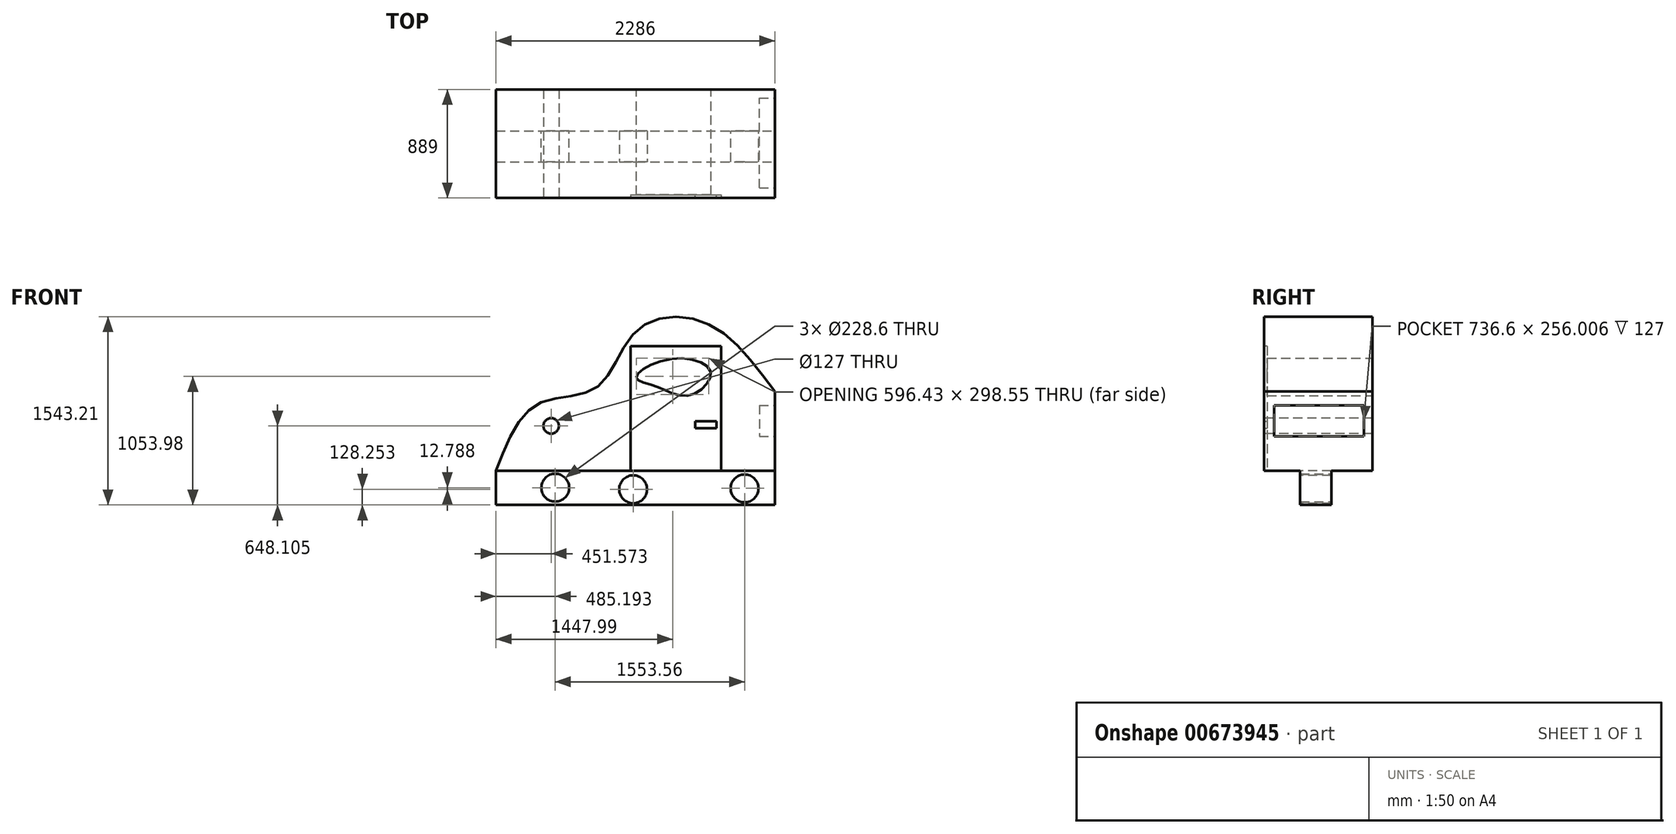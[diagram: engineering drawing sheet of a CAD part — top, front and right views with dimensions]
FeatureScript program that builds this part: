
annotation { "Feature Type Name" : "Feature", "Feature Type Description" : "" }
export const myFeature = defineFeature(function(context is Context, id is Id, definition is map)
    precondition{}
    {
        {
            var Q0;
            Q0=qCreatedBy(makeId("Top.planeOp"),FACE);
            var sketch = newSketch(context, id + "F0", { "sketchPlane" : qUnion([Q0])});
            skLineSegment(sketch, "E0.bottom", {"start": v(-627.65, 592.56) * mm, "end": v(1658.35, 592.56) * mm});
            skLineSegment(sketch, "E0.top", {"start": v(-627.65, -296.44) * mm, "end": v(1658.35, -296.44) * mm});
            skLineSegment(sketch, "E0.left", {"start": v(-627.65, 592.56) * mm, "end": v(-627.65, -296.44) * mm});
            skLineSegment(sketch, "E0.right", {"start": v(1658.35, 592.56) * mm, "end": v(1658.35, -296.44) * mm});
            skSolve(sketch);
        }
        {
            var Q0;
            Q0=makeQuery(id+"F0.imprint","IMPRINT",FACE,{"disambiguationData":[TD([[makeQuery(id+"F0.imprint","IMPRINT",EDGE,{"derivedFrom":sQuery(id+"F0.wireOp",EDGE,"E0.bottom")}),-1.0]])]});
            extrude(context, id + "F1", {"entities" : qUnion([Q0]), "depth" : 1778 * mm, "offsetDistance" : 25.4 * mm});
        }
        {
            var Q0;
            Q0=makeQuery(id+"F1.opExtrude","SWEPT_FACE",FACE,{"disambiguationData":[OSD([sQuery(id+"F0.wireOp",EDGE,"E0.top")])]});
            var sketch = newSketch(context, id + "F2", { "sketchPlane" : qUnion([Q0])});
            skFitSpline(sketch, "E1", {"points": [v(-627.65, 0) * mm, v(-288.97, 545.87) * mm, v(200.39, 685.84) * mm, v(521.68, 1145.9) * mm, v(1081.4, 1218.44) * mm, v(1658.35, 650.05) * mm], "startDerivative": vector(1263.53, 3349.31) * mm, "endDerivative": vector(2269, -3098.13) * mm});
            skSolve(sketch);
        }
        {
            var Q0;
            Q0=makeQuery(id+"F2.imprint","IMPRINT",FACE,{"disambiguationData":[TD([[makeQuery(id+"F2.imprint","IMPRINT",EDGE,{"derivedFrom":sQuery(id+"F2.wireOp",EDGE,"4d44a828-738e-46ed-b581-61caa8d3ac53")}),1.0]])]});
            var Q1;
            {var subQ0=sQuery(id+"F2.wireOp",EDGE,"E1");Q1=makeQuery(id+"F2.imprint","IMPRINT",FACE,{"disambiguationData":[TD([[makeQuery(id+"F2.imprint","IMPRINT",EDGE,{"derivedFrom":subQ0}),1.0]])]});}
            extrude(context, id + "F3", {"entities" : qUnion([Q0, Q1]), "operationType" : NewBodyOperationType.REMOVE, "oppositeDirection" : true, "depth" : 889 * mm, "offsetDistance" : 25.4 * mm});
        }
        {
            var Q0;
            Q0=makeQuery(id+"F1.opExtrude","SWEPT_FACE",FACE,{"disambiguationData":[OSD([sQuery(id+"F0.wireOp",EDGE,"E0.top")])]});
            var sketch = newSketch(context, id + "F4", { "sketchPlane" : qUnion([Q0])});
            skFitSpline(sketch, "E2", {"points": [v(522.12, 767.1) * mm, v(816.35, 920.03) * mm, v(1133.81, 805.82) * mm, v(963.47, 621.93) * mm, v(678.91, 693.55) * mm, v(522.12, 767.1) * mm]});
            skSolve(sketch);
        }
        {
            var Q0;
            Q0=makeQuery(id+"F4.imprint","IMPRINT",FACE,{"disambiguationData":[TD([[makeQuery(id+"F4.imprint","IMPRINT",EDGE,{"derivedFrom":sQuery(id+"F4.wireOp",EDGE,"E2")}),-1.0]])]});
            extrude(context, id + "F5", {"entities" : qUnion([Q0]), "operationType" : NewBodyOperationType.REMOVE, "oppositeDirection" : true, "depth" : 889 * mm, "offsetDistance" : 25.4 * mm});
        }
        {
            var Q0;
            Q0=makeQuery(id+"F1.opExtrude","SWEPT_FACE",FACE,{"disambiguationData":[OSD([sQuery(id+"F0.wireOp",EDGE,"E0.right")])]});
            var sketch = newSketch(context, id + "F6", { "sketchPlane" : qUnion([Q0])});
            skLineSegment(sketch, "E3.bottom", {"start": v(-215.16, 538) * mm, "end": v(521.44, 538) * mm});
            skLineSegment(sketch, "E3.top", {"start": v(-215.16, 282) * mm, "end": v(521.44, 282) * mm});
            skLineSegment(sketch, "E3.left", {"start": v(-215.16, 538) * mm, "end": v(-215.16, 282) * mm});
            skLineSegment(sketch, "E3.right", {"start": v(521.44, 538) * mm, "end": v(521.44, 282) * mm});
            skSolve(sketch);
        }
        {
            var Q0;
            Q0 = qSketchRegion(id + "F6", true);
            extrude(context, id + "F7", {"entities" : qUnion([Q0]), "operationType" : NewBodyOperationType.REMOVE, "oppositeDirection" : true, "depth" : 127 * mm, "offsetDistance" : 25.4 * mm});
        }
        {
            var Q0;
            Q0=makeQuery(id+"F1.opExtrude","CAP_FACE",FACE,{"disambiguationData":[OSD([sQuery(id+"F0.wireOp",EDGE,"E0.bottom"),sQuery(id+"F0.wireOp",EDGE,"E0.top"),sQuery(id+"F0.wireOp",EDGE,"E0.left"),sQuery(id+"F0.wireOp",EDGE,"E0.right")])],"isStart":true});
            var sketch = newSketch(context, id + "F8", { "sketchPlane" : qUnion([Q0])});
            skLineSegment(sketch, "E4.bottom", {"start": v(-627.65, 0) * mm, "end": v(1658.35, 0) * mm});
            skLineSegment(sketch, "E4.top", {"start": v(-627.65, -254.16) * mm, "end": v(1658.35, -254.16) * mm});
            skLineSegment(sketch, "E4.left", {"start": v(-627.65, 0) * mm, "end": v(-627.65, -254.16) * mm});
            skLineSegment(sketch, "E4.right", {"start": v(1658.35, 0) * mm, "end": v(1658.35, -254.16) * mm});
            skSolve(sketch);
        }
        {
            var Q0;
            Q0=makeQuery(id+"F8.imprint","IMPRINT",FACE,{"disambiguationData":[TD([[makeQuery(id+"F8.imprint","IMPRINT",EDGE,{"derivedFrom":sQuery(id+"F8.wireOp",EDGE,"E4.bottom")}),-1.0]])]});
            extrude(context, id + "F9", {"entities" : qUnion([Q0]), "operationType" : NewBodyOperationType.ADD, "depth" : 279.4 * mm, "offsetDistance" : 25.4 * mm});
        }
        {
            var Q0;
            Q0=makeQuery(id+"F9.opExtrude","SWEPT_FACE",FACE,{"disambiguationData":[OSD([sQuery(id+"F8.wireOp",EDGE,"E4.top")])]});
            var sketch = newSketch(context, id + "F10", { "sketchPlane" : qUnion([Q0])});
            skCircle(sketch, "E5", {"center": v(-1411.1, -143.93) * mm, "radius": 114.3 * mm});
            skSolve(sketch);
        }
        {
            var Q0;
            Q0=makeQuery(id+"F10.imprint","IMPRINT",FACE,{"disambiguationData":[TD([[makeQuery(id+"F10.imprint","IMPRINT",EDGE,{"derivedFrom":sQuery(id+"F10.wireOp",EDGE,"E5")}),1.0]])]});
            extrude(context, id + "F11", {"entities" : qUnion([Q0]), "operationType" : NewBodyOperationType.REMOVE, "oppositeDirection" : true, "depth" : 381 * mm, "offsetDistance" : 25.4 * mm});
        }
        {
            var Q0;
            Q0=makeQuery(id+"F9.opExtrude","SWEPT_FACE",FACE,{"disambiguationData":[OSD([sQuery(id+"F8.wireOp",EDGE,"E4.bottom")])]});
            var sketch = newSketch(context, id + "F12", { "sketchPlane" : qUnion([Q0])});
            skCircle(sketch, "E6", {"center": v(496.9, -151.15) * mm, "radius": 114.3 * mm});
            skSolve(sketch);
        }
        {
            var Q0;
            Q0=makeQuery(id+"F12.imprint","IMPRINT",FACE,{"disambiguationData":[TD([[makeQuery(id+"F12.imprint","IMPRINT",EDGE,{"derivedFrom":sQuery(id+"F12.wireOp",EDGE,"E6")}),1.0]])]});
            extrude(context, id + "F13", {"entities" : qUnion([Q0]), "operationType" : NewBodyOperationType.REMOVE, "oppositeDirection" : true, "depth" : 381 * mm, "offsetDistance" : 25.4 * mm});
        }
        {
            var Q0;
            Q0=makeQuery(id+"F1.opExtrude","SWEPT_FACE",FACE,{"disambiguationData":[OSD([sQuery(id+"F0.wireOp",EDGE,"E0.top")])]});
            var sketch = newSketch(context, id + "F14", { "sketchPlane" : qUnion([Q0])});
            skLineSegment(sketch, "E7.bottom", {"start": v(477.06, 1022.97) * mm, "end": v(1218.97, 1022.97) * mm});
            skLineSegment(sketch, "E7.top", {"start": v(477.06, 0) * mm, "end": v(1218.97, 0) * mm});
            skLineSegment(sketch, "E7.left", {"start": v(477.06, 1022.97) * mm, "end": v(477.06, 0) * mm});
            skLineSegment(sketch, "E7.right", {"start": v(1218.97, 1022.97) * mm, "end": v(1218.97, 0) * mm});
            skSolve(sketch);
        }
        {
            var Q0;
            Q0=makeQuery(id+"F14.imprint","IMPRINT",FACE,{"disambiguationData":[TD([[makeQuery(id+"F14.imprint","IMPRINT",EDGE,{"derivedFrom":sQuery(id+"F14.wireOp",EDGE,"E7.bottom")}),-1.0]])]});
            extrude(context, id + "F15", {"entities" : qUnion([Q0]), "operationType" : NewBodyOperationType.REMOVE, "oppositeDirection" : true, "depth" : 25.4 * mm, "offsetDistance" : 25.4 * mm});
        }
        {
            var Q0;
            Q0=makeQuery(id+"F15.boolean.opBoolean","COPY",FACE,{"derivedFrom":makeQuery(id+"F15.opExtrude","CAP_FACE",FACE,{"disambiguationData":[OSD([sQuery(id+"F4.wireOp",EDGE,"E2"),sQuery(id+"F14.wireOp",EDGE,"E7.bottom"),sQuery(id+"F14.wireOp",EDGE,"E7.top"),sQuery(id+"F14.wireOp",EDGE,"E7.left"),sQuery(id+"F14.wireOp",EDGE,"E7.right")])],"isStart":false})});
            var sketch = newSketch(context, id + "F16", { "sketchPlane" : qUnion([Q0])});
            skLineSegment(sketch, "E8.bottom", {"start": v(1004.96, 408.34) * mm, "end": v(1178.93, 408.34) * mm});
            skLineSegment(sketch, "E8.top", {"start": v(1004.96, 348.47) * mm, "end": v(1178.93, 348.47) * mm});
            skLineSegment(sketch, "E8.left", {"start": v(1004.96, 408.34) * mm, "end": v(1004.96, 348.47) * mm});
            skLineSegment(sketch, "E8.right", {"start": v(1178.93, 408.34) * mm, "end": v(1178.93, 348.47) * mm});
            skSolve(sketch);
        }
        {
            var Q0;
            Q0=makeQuery(id+"F16.imprint","IMPRINT",FACE,{"disambiguationData":[TD([[makeQuery(id+"F16.imprint","IMPRINT",EDGE,{"derivedFrom":sQuery(id+"F16.wireOp",EDGE,"E8.bottom")}),-1.0]])]});
            extrude(context, id + "F17", {"entities" : qUnion([Q0]), "operationType" : NewBodyOperationType.ADD, "depth" : 25.4 * mm, "offsetDistance" : 25.4 * mm});
        }
        {
            var Q0;
            Q0=makeQuery(id+"F1.opExtrude","SWEPT_FACE",FACE,{"disambiguationData":[OSD([sQuery(id+"F0.wireOp",EDGE,"E0.top")])]});
            var sketch = newSketch(context, id + "F18", { "sketchPlane" : qUnion([Q0])});
            skCircle(sketch, "E9", {"center": v(-176.08, 368.7) * mm, "radius": 63.5 * mm});
            skSolve(sketch);
        }
        {
            var Q0;
            Q0=makeQuery(id+"F18.imprint","IMPRINT",FACE,{"disambiguationData":[TD([[makeQuery(id+"F18.imprint","IMPRINT",EDGE,{"derivedFrom":sQuery(id+"F18.wireOp",EDGE,"E9")}),1.0]])]});
            extrude(context, id + "F19", {"entities" : qUnion([Q0]), "operationType" : NewBodyOperationType.REMOVE, "oppositeDirection" : true, "depth" : 889 * mm, "offsetDistance" : 25.4 * mm});
        }
        {
            var Q0;
            Q0=makeQuery(id+"F9.opExtrude","SWEPT_FACE",FACE,{"disambiguationData":[OSD([sQuery(id+"F8.wireOp",EDGE,"E4.top")])]});
            var sketch = newSketch(context, id + "F20", { "sketchPlane" : qUnion([Q0])});
            skCircle(sketch, "E10", {"center": v(142.46, -138.36) * mm, "radius": 114.3 * mm});
            skSolve(sketch);
        }
        {
            var Q0;
            Q0=makeQuery(id+"F20.imprint","IMPRINT",FACE,{"disambiguationData":[TD([[makeQuery(id+"F20.imprint","IMPRINT",EDGE,{"derivedFrom":sQuery(id+"F20.wireOp",EDGE,"E10")}),1.0]])]});
            extrude(context, id + "F21", {"entities" : qUnion([Q0]), "operationType" : NewBodyOperationType.REMOVE, "oppositeDirection" : true, "depth" : 381 * mm, "offsetDistance" : 25.4 * mm});
        }
    });
